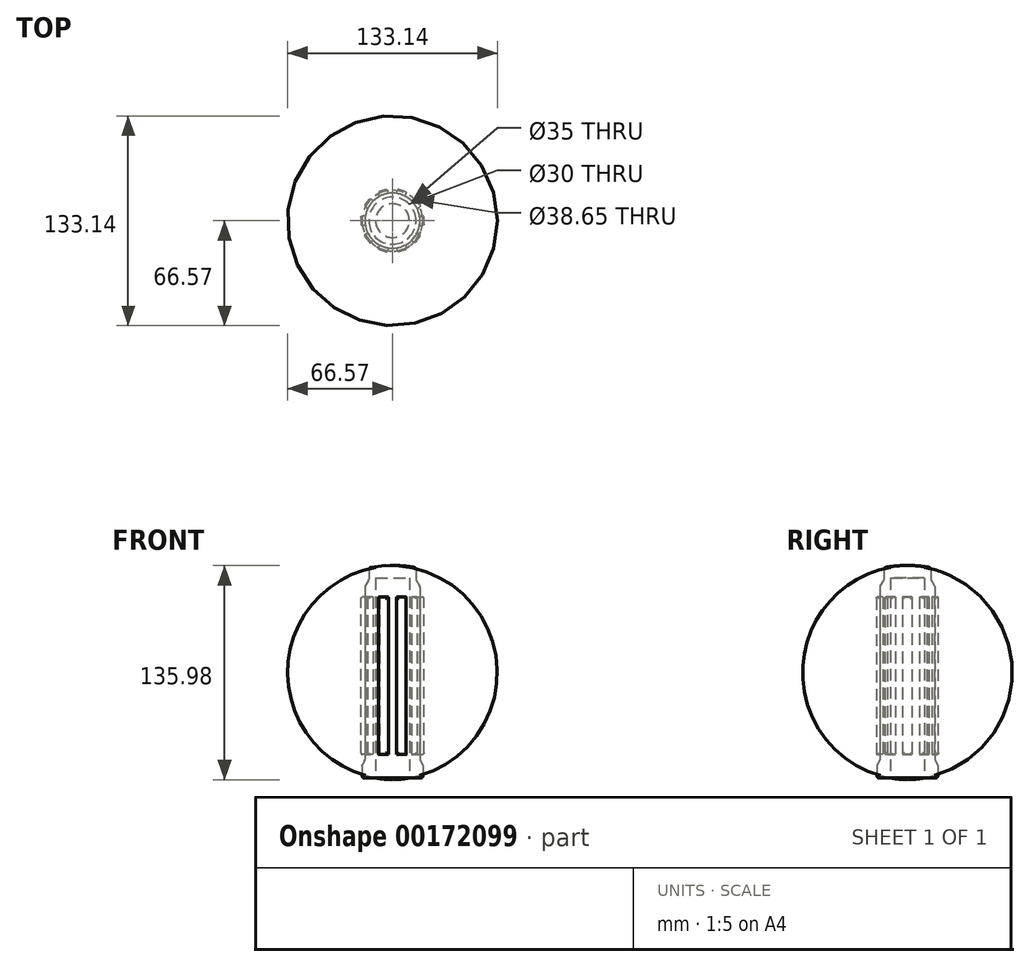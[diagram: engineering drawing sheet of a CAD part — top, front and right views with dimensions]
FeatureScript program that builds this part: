
annotation { "Feature Type Name" : "Feature", "Feature Type Description" : "" }
export const myFeature = defineFeature(function(context is Context, id is Id, definition is map)
    precondition{}
    {
        {
            var Q0;
            Q0=qCreatedBy(makeId("Front.planeOp"),FACE);
            var sketch = newSketch(context, id + "F0", { "sketchPlane" : qUnion([Q0])});
            skLineSegment(sketch, "E0", {"start": v(10.75, 0) * mm, "end": v(19.32, 0) * mm});
            skLineSegment(sketch, "E1", {"start": v(0, -4.96) * mm, "end": v(17.5, -4.96) * mm});
            skLineSegment(sketch, "E2", {"start": v(19.32, 0) * mm, "end": v(19.32, 8) * mm});
            skLineSegment(sketch, "E3", {"start": v(17.5, 11.56) * mm, "end": v(17.5, 121.56) * mm});
            skLineSegment(sketch, "E4", {"start": v(17.5, 11.56) * mm, "end": v(19.32, 8) * mm});
            skLineSegment(sketch, "E5", {"start": v(17.5, 121.56) * mm, "end": v(15, 125.89) * mm});
            skLineSegment(sketch, "E6", {"start": v(15, 133.65) * mm, "end": v(15, 125.89) * mm});
            skLineSegment(sketch, "E7", {"start": v(0, 135) * mm, "end": v(0, 127) * mm});
            skArc(sketch, "E8", {"start": v(15, 133.65) * mm, "mid": v(7.54, 134.74) * mm, "end": v(0, 135) * mm});
            skLineSegment(sketch, "E9", {"start": v(0, 127) * mm, "end": v(10.75, 127) * mm});
            skLineSegment(sketch, "E10", {"start": v(10.75, 127) * mm, "end": v(10.75, 0) * mm});
            skLineSegment(sketch, "E11", {"start": v(0, 0) * mm, "end": v(0, 107.63) * mm, "construction": true});
            skSolve(sketch);
        }
        {
            var Q0;
            Q0 = qSketchRegion(id + "F0", true);
            var Q1;
            Q1=sQuery(id+"F0.wireOp",EDGE,"E11");
            revolve(context, id + "F1", {"entities" : qUnion([Q0]), "axis" : qUnion([Q1]), "revolveType" : RevolveType.FULL});
        }
        {
            var Q0;
            Q0=makeQuery(id+"F1.opRevolve","SWEPT_EDGE",EDGE,{"disambiguationData":[OSD([sQuery(id+"F0.wireOp",EDGE,"E6"),sQuery(id+"F0.wireOp",EDGE,"E8")])]});
            var Q1;
            Q1=makeQuery(id+"F1.opRevolve","SWEPT_EDGE",EDGE,{"disambiguationData":[OSD([sQuery(id+"F0.wireOp",EDGE,"E5"),sQuery(id+"F0.wireOp",EDGE,"E6")])]});
            var Q2;
            Q2=makeQuery(id+"F1.opRevolve","SWEPT_EDGE",EDGE,{"disambiguationData":[OSD([sQuery(id+"F0.wireOp",EDGE,"E3"),sQuery(id+"F0.wireOp",EDGE,"E5")])]});
            var Q3;
            Q3=makeQuery(id+"F1.opRevolve","SWEPT_EDGE",EDGE,{"disambiguationData":[OSD([sQuery(id+"F0.wireOp",EDGE,"E3"),sQuery(id+"F0.wireOp",EDGE,"E4")])]});
            var Q4;
            Q4=makeQuery(id+"F1.opRevolve","SWEPT_EDGE",EDGE,{"disambiguationData":[OSD([sQuery(id+"F0.wireOp",EDGE,"E2"),sQuery(id+"F0.wireOp",EDGE,"E4")])]});
            var Q5;
            Q5=makeQuery(id+"F1.opRevolve","SWEPT_EDGE",EDGE,{"disambiguationData":[OSD([sQuery(id+"F0.wireOp",EDGE,"E0"),sQuery(id+"F0.wireOp",EDGE,"E2")])]});
            fillet(context, id + "F2", {"entities" : qUnion([Q0, Q1, Q2, Q3, Q4, Q5]), "radius" : 1.6 * mm, "tangentPropagation" : true, "allowEdgeOverflow" : false});
        }
        {
            var Q0;
            Q0=qCreatedBy(makeId("Right.planeOp"),FACE);
            cPlane(context, id + "F3", {"entities" : qUnion([Q0]), "cplaneType" : CPlaneType.OFFSET, "offset" : 20 * mm, "width" : 150 * mm, "height" : 150 * mm});
        }
        {
            var Q0;
            Q0=qCreatedBy(id+"F3.planeOp",FACE);
            var sketch = newSketch(context, id + "F4", { "sketchPlane" : qUnion([Q0])});
            skLineSegment(sketch, "E12.bottom", {"start": v(-3, 15) * mm, "end": v(3, 15) * mm});
            skLineSegment(sketch, "E12.top", {"start": v(-3, 115) * mm, "end": v(3, 115) * mm});
            skLineSegment(sketch, "E12.left", {"start": v(-3, 15) * mm, "end": v(-3, 115) * mm});
            skLineSegment(sketch, "E12.right", {"start": v(3, 15) * mm, "end": v(3, 115) * mm});
            skSolve(sketch);
        }
        {
            var Q0;
            Q0 = qSketchRegion(id + "F4", true);
            var Q1;
            Q1=makeQuery(id+"F1.opRevolve","SWEPT_FACE",FACE,{"disambiguationData":[OSD([sQuery(id+"F0.wireOp",EDGE,"E3")])]});
            extrude(context, id + "F5", {"entities" : qUnion([Q0]), "endBound" : BoundingType.UP_TO_SURFACE, "oppositeDirection" : true, "endBoundEntityFace" : qUnion([Q1]), "depth" : 25 * mm});
        }
        {
            var Q0;
            Q0=makeQuery(id+"F5.opExtrude","CAP_EDGE",EDGE,{"disambiguationData":[OSD([sQuery(id+"F4.wireOp",EDGE,"E12.left")])],"isStart":true});
            var Q1;
            Q1=makeQuery(id+"F5.opExtrude","CAP_EDGE",EDGE,{"disambiguationData":[OSD([sQuery(id+"F4.wireOp",EDGE,"E12.top")])],"isStart":true});
            var Q2;
            Q2=makeQuery(id+"F5.opExtrude","CAP_EDGE",EDGE,{"disambiguationData":[OSD([sQuery(id+"F4.wireOp",EDGE,"E12.right")])],"isStart":true});
            var Q3;
            Q3=makeQuery(id+"F5.opExtrude","CAP_EDGE",EDGE,{"disambiguationData":[OSD([sQuery(id+"F4.wireOp",EDGE,"E12.bottom")])],"isStart":true});
            var Q4;
            Q4=makeQuery(id+"F5.opExtrude","TWEAK_EDGE",EDGE,{"derivedFrom":[makeQuery(id+"F1.opRevolve","SWEPT_FACE",FACE,{"disambiguationData":[OSD([sQuery(id+"F0.wireOp",EDGE,"E3")])]}),makeQuery(id+"F4.imprint","IMPRINT",EDGE,{"derivedFrom":sQuery(id+"F4.wireOp",EDGE,"E12.right")})]});
            var Q5;
            Q5=makeQuery(id+"F5.opExtrude","TWEAK_EDGE",EDGE,{"derivedFrom":[makeQuery(id+"F1.opRevolve","SWEPT_FACE",FACE,{"disambiguationData":[OSD([sQuery(id+"F0.wireOp",EDGE,"E3")])]}),makeQuery(id+"F4.imprint","IMPRINT",EDGE,{"derivedFrom":sQuery(id+"F4.wireOp",EDGE,"E12.left")})]});
            var Q6;
            Q6=makeQuery(id+"F5.opExtrude","TWEAK_EDGE",EDGE,{"derivedFrom":[makeQuery(id+"F1.opRevolve","SWEPT_FACE",FACE,{"disambiguationData":[OSD([sQuery(id+"F0.wireOp",EDGE,"E3")])]}),makeQuery(id+"F4.imprint","IMPRINT",EDGE,{"derivedFrom":sQuery(id+"F4.wireOp",EDGE,"E12.top")})]});
            var Q7;
            Q7=makeQuery(id+"F5.opExtrude","TWEAK_EDGE",EDGE,{"derivedFrom":[makeQuery(id+"F1.opRevolve","SWEPT_FACE",FACE,{"disambiguationData":[OSD([sQuery(id+"F0.wireOp",EDGE,"E3")])]}),makeQuery(id+"F4.imprint","IMPRINT",EDGE,{"derivedFrom":sQuery(id+"F4.wireOp",EDGE,"E12.bottom")})]});
            fillet(context, id + "F6", {"entities" : qUnion([Q0, Q1, Q2, Q3, Q4, Q5, Q6, Q7]), "radius" : 1 * mm, "tangentPropagation" : true, "allowEdgeOverflow" : false});
        }
        {
            var Q0;
            Q0=makeQuery(id+"F5.opExtrude","SWEPT_BODY",BODY,{"disambiguationData":[OSD([sQuery(id+"F4.wireOp",EDGE,"E12.bottom"),sQuery(id+"F4.wireOp",EDGE,"E12.top"),sQuery(id+"F4.wireOp",EDGE,"E12.left"),sQuery(id+"F4.wireOp",EDGE,"E12.right")])]});
            var Q1;
            Q1=sQuery(id+"F0.wireOp",EDGE,"E11");
            circularPattern(context, id + "F7", {"entities" : qUnion([Q0]), "axis" : qUnion([Q1]), "angle" : 360 * degree, "instanceCount" : 10, "equalSpace" : true});
        }
    });
